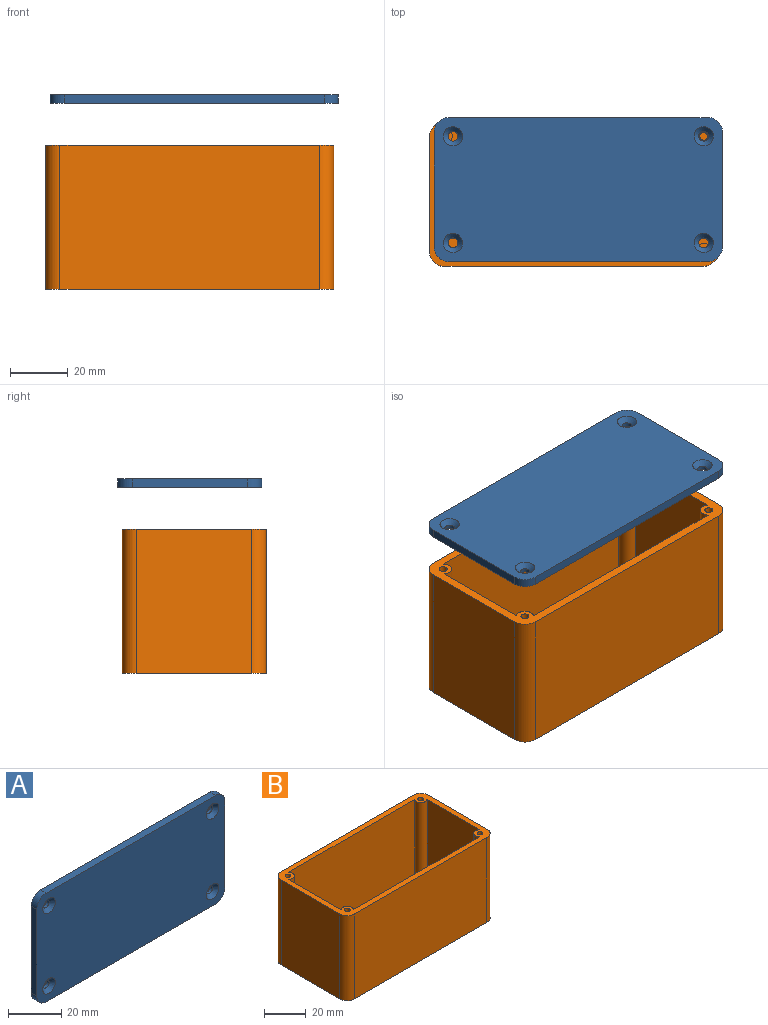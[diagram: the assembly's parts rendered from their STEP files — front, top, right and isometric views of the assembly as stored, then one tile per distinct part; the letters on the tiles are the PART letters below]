
ASSEMBLY  parts=2 mates=1
PART A: 18 faces, bbox 100x3x50 mm
  f0: plane 40x3mm, normal (1,0,0), area 120mm2, adj f4,f5,f6,f9
  f1: plane 90x3mm, normal (0,0,1), area 270mm2, adj f4,f5,f6,f7
  f2: plane 40x3mm, normal (-1,0,0), area 120mm2, adj f4,f5,f7,f8
  f3: plane 90x3mm, normal (0,0,-1), area 270mm2, adj f4,f5,f8,f9
  f4: plane 100x50mm, normal (0,-1,0), area 4836.7mm2, adj f0,f1,f2,f3,f6,f7,f8,f9
  f5: plane 100x50mm, normal (0,1,0), area 4942.2mm2, adj f0,f1,f2,f3,f6,f7,f8,f9
  f6: cylinder r=5mm len=5mm, axis (0,-1,0), area 23.6mm2, adj f0,f1,f4,f5
  f7: cylinder r=5mm len=5mm, axis (0,1,0), area 23.6mm2, adj f1,f2,f4,f5
  f8: cylinder r=5mm len=5mm, axis (0,-1,0), area 23.6mm2, adj f2,f3,f4,f5
  f9: cylinder r=5mm len=5mm, axis (0,1,0), area 23.6mm2, adj f0,f3,f4,f5
  f10: cylinder r=1.7mm len=3.4mm, axis (0,-1,0), area 14.3mm2, adj f5,f11
  f11: cone r=1.7mm half-angle=45deg, axis (0,-1,0), area 37.3mm2, adj f4,f10
  f12: cylinder r=1.7mm len=3.4mm, axis (0,-1,0), area 14.3mm2, adj f5,f13
  f13: cone r=1.7mm half-angle=45deg, axis (0,-1,0), area 37.3mm2, adj f4,f12
  f14: cylinder r=1.7mm len=3.4mm, axis (0,-1,0), area 14.3mm2, adj f5,f15
  f15: cone r=1.7mm half-angle=45deg, axis (0,-1,0), area 37.3mm2, adj f4,f14
  f16: cylinder r=1.7mm len=3.4mm, axis (0,-1,0), area 14.3mm2, adj f5,f17
  f17: cone r=1.7mm half-angle=45deg, axis (0,-1,0), area 37.3mm2, adj f4,f16
PART B: 27 faces, bbox 100x50x50 mm
  f0: plane 94x44mm, normal (0,0,1), area 4050.6mm2, adj f1,f2,f3,f4,f15,f18,f21,f24
  f1: plane 85.61x47mm, normal (0,-1,0), area 4023.6mm2, adj f0,f9,f15,f24
  f2: plane 47x35.5mm, normal (-1,0,0), area 1668.4mm2, adj f0,f9,f21,f24
  f3: plane 85.61x47mm, normal (0,1,0), area 4023.6mm2, adj f0,f9,f18,f21
  f4: plane 47x35.5mm, normal (1,0,0), area 1668.4mm2, adj f0,f9,f15,f18
  f5: plane 50x40mm, normal (1,0,0), area 2000mm2, adj f9,f10,f11,f14
  f6: plane 90x50mm, normal (0,1,0), area 4500mm2, adj f9,f10,f11,f12
  f7: plane 50x40mm, normal (-1,0,0), area 2000mm2, adj f9,f10,f12,f13
  f8: plane 90x50mm, normal (0,-1,0), area 4500mm2, adj f9,f10,f13,f14
  f9: plane 100x50mm, normal (0,0,1), area 904.1mm2, adj f1,f2,f3,f4,f5,f6,f7,f8
  f10: plane 100x50mm, normal (0,0,-1), area 4978.5mm2, adj f5,f6,f7,f8,f11,f12,f13,f14
  f11: cylinder r=5mm len=50mm, axis (0,0,1), area 392.7mm2, adj f5,f6,f9,f10
  f12: cylinder r=5mm len=50mm, axis (0,0,-1), area 392.7mm2, adj f6,f7,f9,f10
  f13: cylinder r=5mm len=50mm, axis (0,0,1), area 392.7mm2, adj f7,f8,f9,f10
  f14: cylinder r=5mm len=50mm, axis (0,0,-1), area 392.7mm2, adj f5,f8,f9,f10
  f15: cylinder r=3mm len=47mm, axis (0,0,-1), area 416mm2, adj f0,f1,f4,f9
  f16: cylinder r=1.38mm len=47mm, axis (0,0,-1), area 406.1mm2, adj f9,f17
  f17: plane 2.75x2.75mm, normal (0,0,1), area 5.9mm2, adj f16
  f18: cylinder r=3mm len=47mm, axis (0,0,-1), area 416mm2, adj f0,f3,f4,f9
  f19: cylinder r=1.38mm len=47mm, axis (0,0,-1), area 406.1mm2, adj f9,f20
  f20: plane 2.75x2.75mm, normal (0,0,1), area 5.9mm2, adj f19
  f21: cylinder r=3mm len=47mm, axis (0,0,-1), area 416mm2, adj f0,f2,f3,f9
  f22: cylinder r=1.38mm len=47mm, axis (0,0,-1), area 406.1mm2, adj f9,f23
  f23: plane 2.75x2.75mm, normal (0,0,1), area 5.9mm2, adj f22
  f24: cylinder r=3mm len=47mm, axis (0,0,-1), area 416mm2, adj f0,f1,f2,f9
  f25: cylinder r=1.38mm len=47mm, axis (0,0,-1), area 406.1mm2, adj f9,f26
  f26: plane 2.75x2.75mm, normal (0,0,1), area 5.9mm2, adj f25
PLACE A rot(axis=(-1,0,0),90deg) t=(-23.01,-104.85,81.19)mm
PLACE B t=(-24.61,-106.42,16.76)mm fixed
MATE slider A.f12 <-> B.f24  axis (0,0,1) through (20.49,-86.35,84.19)mm
